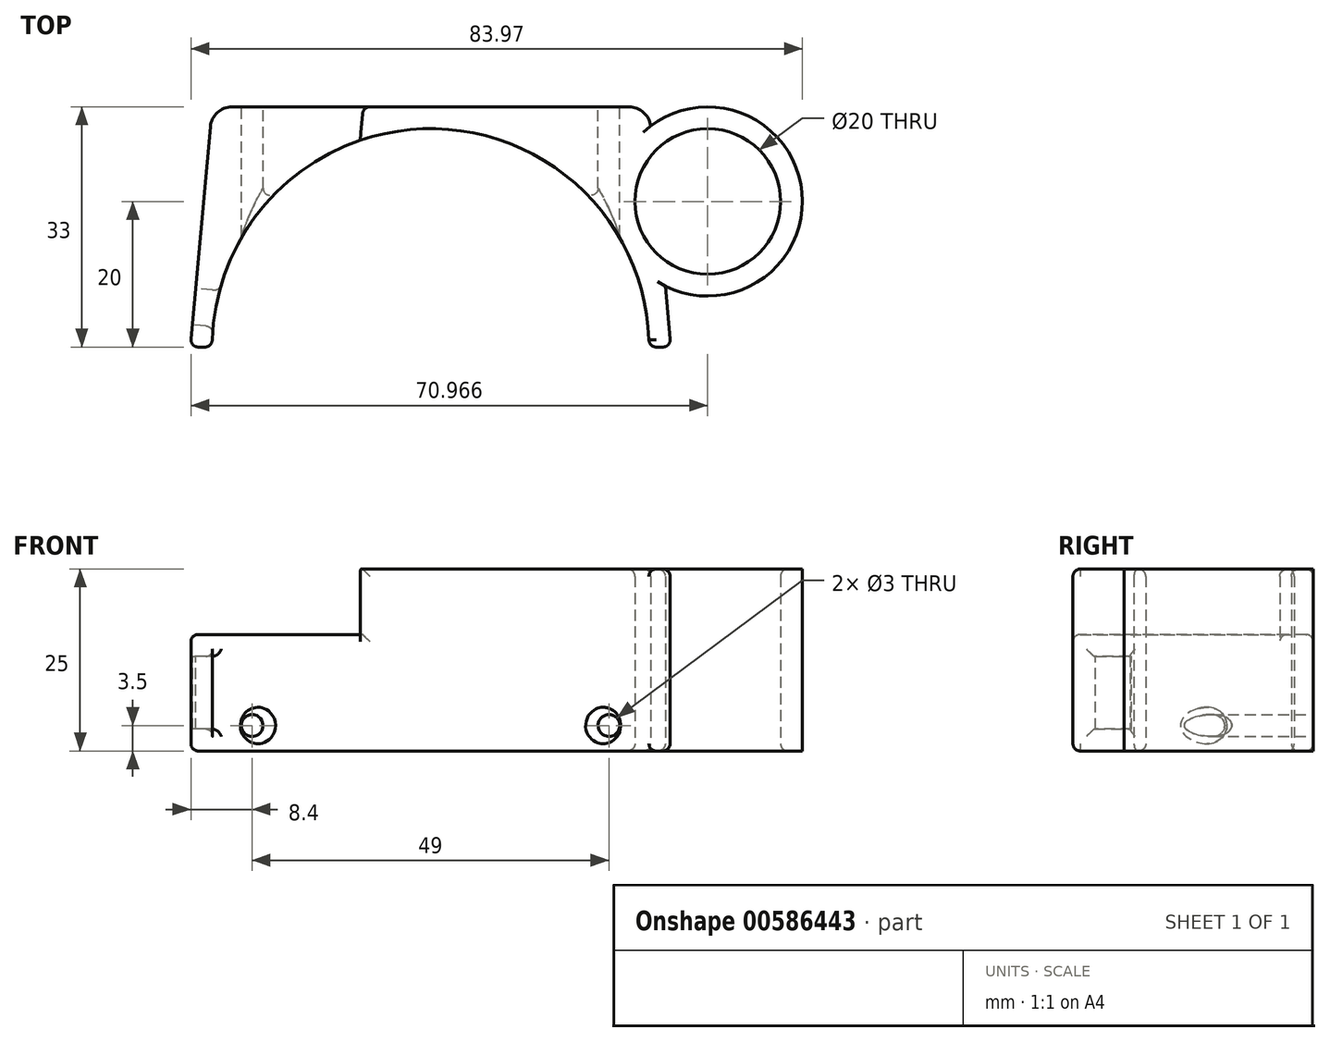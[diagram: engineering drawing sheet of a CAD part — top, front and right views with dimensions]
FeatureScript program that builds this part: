
annotation { "Feature Type Name" : "Feature", "Feature Type Description" : "" }
export const myFeature = defineFeature(function(context is Context, id is Id, definition is map)
    precondition{}
    {
        {
            var Q0;
            Q0=qCreatedBy(makeId("Top.planeOp"),FACE);
            var sketch = newSketch(context, id + "F0", { "sketchPlane" : qUnion([Q0])});
            skArc(sketch, "E0", {"start": v(29.98, 0.97) * mm, "mid": v(0, 30) * mm, "end": v(-29.98, 0.97) * mm});
            skLineSegment(sketch, "E1", {"start": v(0, 33) * mm, "end": v(-27.26, 33) * mm});
            skLineSegment(sketch, "E2", {"start": v(0, 33) * mm, "end": v(27.26, 33) * mm});
            skLineSegment(sketch, "E3", {"start": v(-30.98, 0) * mm, "end": v(-31.9, 0) * mm});
            skLineSegment(sketch, "E4", {"start": v(30.98, 0) * mm, "end": v(31.9, 0) * mm});
            skLineSegment(sketch, "E5", {"start": v(-30.25, 30.27) * mm, "end": v(-32.9, 1.1) * mm});
            skPoint(sketch, "E6.visualSharp", {"position": v(-30, 33) * mm});
            skArc(sketch, "E6.filletArc", {"start": v(-27.26, 33) * mm, "mid": v(-29.28, 32.22) * mm, "end": v(-30.25, 30.27) * mm});
            skPoint(sketch, "E7.visualSharp", {"position": v(30, 33) * mm});
            skArc(sketch, "E7.filletArc", {"start": v(30.24, 30.38) * mm, "mid": v(29.24, 32.25) * mm, "end": v(27.26, 33) * mm});
            skPoint(sketch, "E8.visualSharp", {"position": v(-33, 0) * mm});
            skArc(sketch, "E8.filletArc", {"start": v(-32.9, 1.1) * mm, "mid": v(-32.64, 0.33) * mm, "end": v(-31.9, 0) * mm});
            skPoint(sketch, "E9.visualSharp", {"position": v(-30, 0) * mm});
            skArc(sketch, "E9.filletArc", {"start": v(-30.98, 0) * mm, "mid": v(-30.29, 0.28) * mm, "end": v(-29.98, 0.97) * mm});
            skPoint(sketch, "E10.visualSharp", {"position": v(30, 0) * mm});
            skArc(sketch, "E10.filletArc", {"start": v(29.98, 0.97) * mm, "mid": v(30.29, 0.28) * mm, "end": v(30.98, 0) * mm});
            skPoint(sketch, "E11.visualSharp", {"position": v(33, 0) * mm});
            skArc(sketch, "E11.filletArc", {"start": v(31.9, 0) * mm, "mid": v(32.64, 0.33) * mm, "end": v(32.9, 1.1) * mm});
            skCircle(sketch, "E12", {"center": v(38.07, 20) * mm, "radius": 10 * mm});
            skArc(sketch, "E13.0", {"start": v(32.24, 8.38) * mm, "mid": v(51.01, 21.18) * mm, "end": v(30.24, 30.38) * mm});
            skLineSegment(sketch, "E14.trimOffspring", {"start": v(32.24, 8.38) * mm, "end": v(32.9, 1.1) * mm});
            skSolve(sketch);
        }
        {
            var Q0;
            Q0 = qSketchRegion(id + "F0", true);
            extrude(context, id + "F1", {"entities" : qUnion([Q0]), "depth" : 25 * mm, "offsetDistance" : 25 * mm});
        }
        {
            var Q0;
            Q0=makeQuery(id+"F1.opExtrude","SWEPT_FACE",FACE,{"disambiguationData":[OSD([sQuery(id+"F0.wireOp",EDGE,"E1"),sQuery(id+"F0.wireOp",EDGE,"E2")])]});
            var sketch = newSketch(context, id + "F2", { "sketchPlane" : qUnion([Q0])});
            skPoint(sketch, "E15.endSnap0", {"position": v(0, 21.5) * mm});
            skCircle(sketch, "E16", {"center": v(24.5, 3.5) * mm, "radius": 1.5 * mm});
            skCircle(sketch, "E17", {"center": v(-24.5, 3.5) * mm, "radius": 1.5 * mm});
            skSolve(sketch);
        }
        {
            var Q0;
            Q0 = qSketchRegion(id + "F2", true);
            extrude(context, id + "F3", {"entities" : qUnion([Q0]), "operationType" : NewBodyOperationType.REMOVE, "endBound" : BoundingType.THROUGH_ALL, "oppositeDirection" : true, "depth" : 25 * mm, "offsetDistance" : 25 * mm});
        }
        {
            var Q0;
            Q0=makeQuery(id+"F1.opExtrude","SWEPT_FACE",FACE,{"disambiguationData":[OSD([sQuery(id+"F0.wireOp",EDGE,"E5")])]});
            var sketch = newSketch(context, id + "F4", { "sketchPlane" : qUnion([Q0])});
            skLineSegment(sketch, "E18", {"start": v(1.9, 16) * mm, "end": v(-27.4, 16) * mm});
            skSolve(sketch);
        }
        {
            var Q0;
            {var subQ0=sQuery(id+"F4.wireOp",EDGE,"E18");Q0=makeQuery(id+"F4.imprint","IMPRINT",FACE,{"disambiguationData":[TD([[makeQuery(id+"F4.imprint","IMPRINT",EDGE,{"derivedFrom":subQ0}),-1.0]])]});}
            extrude(context, id + "F5", {"entities" : qUnion([Q0]), "operationType" : NewBodyOperationType.REMOVE, "endBound" : BoundingType.UP_TO_NEXT, "oppositeDirection" : true, "depth" : 25 * mm, "offsetDistance" : 25 * mm});
        }
        {
            var Q0;
            Q0=makeQuery(id+"F5.boolean.opBoolean","COPY",FACE,{"derivedFrom":makeQuery(id+"F5.opExtrude","SWEPT_FACE",FACE,{"disambiguationData":[OSD([sQuery(id+"F0.wireOp",EDGE,"E5"),sQuery(id+"F0.wireOp",EDGE,"E8.filletArc")])]})});
            extrude(context, id + "F6", {"entities" : qUnion([Q0]), "operationType" : NewBodyOperationType.REMOVE, "oppositeDirection" : true, "depth" : 25 * mm, "offsetDistance" : 25 * mm});
        }
        {
            var Q0;
            Q0=makeQuery(id+"F5.boolean.opBoolean","COPY",FACE,{"derivedFrom":makeQuery(id+"F5.opExtrude","SWEPT_FACE",FACE,{"disambiguationData":[OSD([sQuery(id+"F0.wireOp",EDGE,"E5"),sQuery(id+"F0.wireOp",EDGE,"E6.filletArc")])]})});
            extrude(context, id + "F7", {"entities" : qUnion([Q0]), "operationType" : NewBodyOperationType.REMOVE, "oppositeDirection" : true, "depth" : 25 * mm, "offsetDistance" : 25 * mm});
        }
        {
            var Q0;
            Q0=makeQuery(id+"F1.opExtrude","CAP_EDGE",EDGE,{"disambiguationData":[OSD([sQuery(id+"F0.wireOp",EDGE,"E0")])],"isStart":false});
            var Q1;
            Q1=makeQuery(id+"F1.opExtrude","CAP_EDGE",EDGE,{"disambiguationData":[OSD([sQuery(id+"F0.wireOp",EDGE,"E1"),sQuery(id+"F0.wireOp",EDGE,"E2")])],"isStart":false});
            var Q2;
            Q2=makeQuery(id+"F1.opExtrude","CAP_EDGE",EDGE,{"disambiguationData":[OSD([sQuery(id+"F0.wireOp",EDGE,"E12")])],"isStart":false});
            var Q3;
            Q3=makeQuery(id+"F5.boolean.opBoolean","COPY",EDGE,{"derivedFrom":makeQuery(id+"F5.opExtrude","CAP_EDGE",EDGE,{"disambiguationData":[OSD([sQuery(id+"F4.wireOp",EDGE,"E18")]),topologyDisambiguationEdgeConnected([makeQuery(id+"F1.opExtrude","SWEPT_FACE",FACE,{"disambiguationData":[OSD([sQuery(id+"F0.wireOp",EDGE,"E0")])]})])],"isStart":false})});
            var Q4;
            Q4=makeQuery(id+"F7.boolean.opBoolean","INTERSECT",EDGE,{"derivedFrom":[makeQuery(id+"F1.opExtrude","SWEPT_FACE",FACE,{"disambiguationData":[OSD([sQuery(id+"F0.wireOp",EDGE,"E1"),sQuery(id+"F0.wireOp",EDGE,"E2")])]}),makeQuery(id+"F7.opExtrude","SWEPT_FACE",FACE,{"disambiguationData":[OSD([sQuery(id+"F0.wireOp",EDGE,"E5"),sQuery(id+"F0.wireOp",EDGE,"E6.filletArc"),sQuery(id+"F4.wireOp",EDGE,"E18")])]})]});
            var Q5;
            Q5=makeQuery(id+"F7.boolean.opBoolean","COPY",EDGE,{"derivedFrom":makeQuery(id+"F7.opExtrude","SWEPT_EDGE",EDGE,{"disambiguationData":[OSD([sQuery(id+"F0.wireOp",EDGE,"E0"),sQuery(id+"F0.wireOp",EDGE,"E5"),sQuery(id+"F0.wireOp",EDGE,"E6.filletArc"),sQuery(id+"F0.wireOp",EDGE,"E9.filletArc")])]})});
            var Q6;
            {var subQ0=sQuery(id+"F0.wireOp",EDGE,"E6.filletArc");var subQ1=sQuery(id+"F0.wireOp",EDGE,"E5");var subQ2=makeQuery(id+"F5.boolean.opBoolean","COPY",EDGE,{"derivedFrom":makeQuery(id+"F5.opExtrude","CAP_EDGE",EDGE,{"disambiguationData":[OSD([subQ1,subQ0])],"isStart":false})});Q6=makeQuery(id+"F7.boolean.opBoolean","MERGE",EDGE,{"derivedFrom":[subQ2],"fromTools":[makeQuery(id+"F7.opExtrude","CAP_EDGE",EDGE,{"disambiguationData":[OSD([subQ1,subQ0]),TDD([subQ2])],"isStart":true})]});}
            var Q7;
            Q7=makeQuery(id+"F7.boolean.opBoolean","INTERSECT",EDGE,{"derivedFrom":[makeQuery(id+"F1.opExtrude","SWEPT_FACE",FACE,{"disambiguationData":[OSD([sQuery(id+"F0.wireOp",EDGE,"E1"),sQuery(id+"F0.wireOp",EDGE,"E2")])]}),makeQuery(id+"F7.opExtrude","SWEPT_FACE",FACE,{"disambiguationData":[OSD([sQuery(id+"F0.wireOp",EDGE,"E0"),sQuery(id+"F0.wireOp",EDGE,"E5"),sQuery(id+"F0.wireOp",EDGE,"E6.filletArc")])]})]});
            var Q8;
            Q8=makeQuery(id+"F1.opExtrude","CAP_EDGE",EDGE,{"disambiguationData":[OSD([sQuery(id+"F0.wireOp",EDGE,"E1"),sQuery(id+"F0.wireOp",EDGE,"E2")])],"isStart":true});
            var Q9;
            Q9=makeQuery(id+"F1.opExtrude","CAP_EDGE",EDGE,{"disambiguationData":[OSD([sQuery(id+"F0.wireOp",EDGE,"E12")])],"isStart":true});
            var Q10;
            Q10=makeQuery(id+"F3.boolean.opBoolean","COPY",EDGE,{"derivedFrom":makeQuery(id+"F3.opExtrude","CAP_EDGE",EDGE,{"disambiguationData":[OSD([sQuery(id+"F2.wireOp",EDGE,"E17")])],"isStart":true})});
            var Q11;
            Q11=makeQuery(id+"F3.boolean.opBoolean","COPY",EDGE,{"derivedFrom":makeQuery(id+"F3.opExtrude","CAP_EDGE",EDGE,{"disambiguationData":[OSD([sQuery(id+"F2.wireOp",EDGE,"E16")])],"isStart":true})});
            var Q12;
            Q12=makeQuery(id+"F3.boolean.opBoolean","INTERSECT",EDGE,{"derivedFrom":[makeQuery(id+"F1.opExtrude","SWEPT_FACE",FACE,{"disambiguationData":[OSD([sQuery(id+"F0.wireOp",EDGE,"E0")])]}),makeQuery(id+"F3.opExtrude","SWEPT_FACE",FACE,{"disambiguationData":[OSD([sQuery(id+"F2.wireOp",EDGE,"E17")])]})]});
            var Q13;
            Q13=makeQuery(id+"F3.boolean.opBoolean","INTERSECT",EDGE,{"derivedFrom":[makeQuery(id+"F1.opExtrude","SWEPT_FACE",FACE,{"disambiguationData":[OSD([sQuery(id+"F0.wireOp",EDGE,"E0")])]}),makeQuery(id+"F3.opExtrude","SWEPT_FACE",FACE,{"disambiguationData":[OSD([sQuery(id+"F2.wireOp",EDGE,"E16")])]})]});
            fillet(context, id + "F8", {"entities" : qUnion([Q0, Q1, Q2, Q3, Q4, Q5, Q6, Q7, Q8, Q9, Q10, Q11, Q12, Q13]), "radius" : 1 * mm, "tangentPropagation" : true, "allowEdgeOverflow" : false});
        }
        {
            var Q0;
            Q0=makeQuery(id+"F1.opExtrude","SWEPT_FACE",FACE,{"disambiguationData":[OSD([sQuery(id+"F0.wireOp",EDGE,"E5")])]});
            var sketch = newSketch(context, id + "F9", { "sketchPlane" : qUnion([Q0])});
            skLineSegment(sketch, "E19.0", {"start": v(-0.1, 3) * mm, "end": v(-0.1, 13) * mm});
            skLineSegment(sketch, "E19.1", {"start": v(-5.1, 3) * mm, "end": v(-0.1, 3) * mm});
            skLineSegment(sketch, "E19.3", {"start": v(-0.1, 13) * mm, "end": v(-5.1, 13) * mm});
            skLineSegment(sketch, "E20.0", {"start": v(-5.1, 3) * mm, "end": v(-5.1, 13) * mm});
            skSolve(sketch);
        }
        {
            var Q0;
            Q0=makeQuery(id+"F9.imprint","IMPRINT",FACE,{"disambiguationData":[TD([[makeQuery(id+"F9.imprint","IMPRINT",EDGE,{"derivedFrom":sQuery(id+"F9.wireOp",EDGE,"E19.0")}),1.0]])]});
            extrude(context, id + "F10", {"entities" : qUnion([Q0]), "operationType" : NewBodyOperationType.REMOVE, "oppositeDirection" : true, "depth" : 25 * mm, "offsetDistance" : 25 * mm});
        }
        {
            var Q0;
            Q0=makeQuery(id+"F10.boolean.opBoolean","COPY",EDGE,{"derivedFrom":makeQuery(id+"F10.opExtrude","CAP_EDGE",EDGE,{"disambiguationData":[OSD([sQuery(id+"F9.wireOp",EDGE,"E19.1")])],"isStart":true})});
            var Q1;
            Q1=makeQuery(id+"F10.boolean.opBoolean","INTERSECT",EDGE,{"derivedFrom":[makeQuery(id+"F1.opExtrude","SWEPT_FACE",FACE,{"disambiguationData":[OSD([sQuery(id+"F0.wireOp",EDGE,"E0")])]}),makeQuery(id+"F10.opExtrude","SWEPT_FACE",FACE,{"disambiguationData":[OSD([sQuery(id+"F9.wireOp",EDGE,"E19.0")])]})]});
            var Q2;
            Q2=makeQuery(id+"F10.boolean.opBoolean","COPY",EDGE,{"derivedFrom":makeQuery(id+"F10.opExtrude","CAP_EDGE",EDGE,{"disambiguationData":[OSD([sQuery(id+"F9.wireOp",EDGE,"E19.0")])],"isStart":true})});
            var Q3;
            Q3=makeQuery(id+"F10.boolean.opBoolean","COPY",EDGE,{"derivedFrom":makeQuery(id+"F10.opExtrude","CAP_EDGE",EDGE,{"disambiguationData":[OSD([sQuery(id+"F9.wireOp",EDGE,"E20.0")])],"isStart":true})});
            var Q4;
            Q4=makeQuery(id+"F10.boolean.opBoolean","COPY",EDGE,{"derivedFrom":makeQuery(id+"F10.opExtrude","CAP_EDGE",EDGE,{"disambiguationData":[OSD([sQuery(id+"F9.wireOp",EDGE,"E19.3")])],"isStart":true})});
            var Q5;
            Q5=makeQuery(id+"F10.boolean.opBoolean","INTERSECT",EDGE,{"derivedFrom":[makeQuery(id+"F1.opExtrude","SWEPT_FACE",FACE,{"disambiguationData":[OSD([sQuery(id+"F0.wireOp",EDGE,"E0")])]}),makeQuery(id+"F10.opExtrude","SWEPT_FACE",FACE,{"disambiguationData":[OSD([sQuery(id+"F9.wireOp",EDGE,"E19.3")])]})]});
            var Q6;
            Q6=makeQuery(id+"F10.boolean.opBoolean","INTERSECT",EDGE,{"derivedFrom":[makeQuery(id+"F1.opExtrude","SWEPT_FACE",FACE,{"disambiguationData":[OSD([sQuery(id+"F0.wireOp",EDGE,"E0")])]}),makeQuery(id+"F10.opExtrude","SWEPT_FACE",FACE,{"disambiguationData":[OSD([sQuery(id+"F9.wireOp",EDGE,"E20.0")])]})]});
            var Q7;
            Q7=makeQuery(id+"F10.boolean.opBoolean","INTERSECT",EDGE,{"derivedFrom":[makeQuery(id+"F1.opExtrude","SWEPT_FACE",FACE,{"disambiguationData":[OSD([sQuery(id+"F0.wireOp",EDGE,"E0")])]}),makeQuery(id+"F10.opExtrude","SWEPT_FACE",FACE,{"disambiguationData":[OSD([sQuery(id+"F9.wireOp",EDGE,"E19.1")])]})]});
            fillet(context, id + "F11", {"entities" : qUnion([Q0, Q1, Q2, Q3, Q4, Q5, Q6, Q7]), "radius" : 1 * mm, "tangentPropagation" : true, "allowEdgeOverflow" : false});
        }
    });
